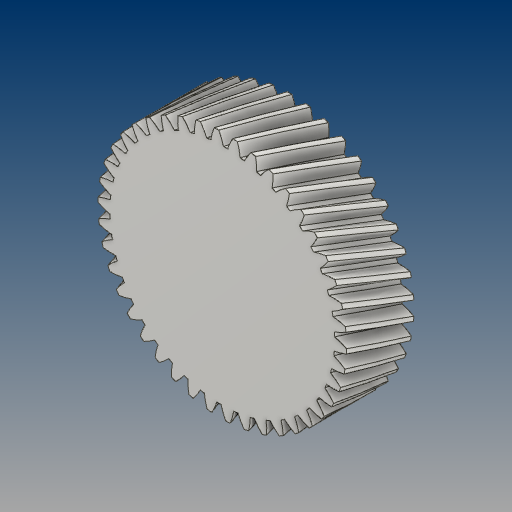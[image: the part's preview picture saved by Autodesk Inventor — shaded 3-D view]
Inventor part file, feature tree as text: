
AUTODESK INVENTOR PART (.ipt)
format: ipt  version: 2021 (Build 250183000, 183)  size: 704,512 bytes
history: native  units: mm (DEFAULTED — no unit token found)
features: plane x3, other x3, sketch x2, extrude x1
ambient origin geometry x8: Origin, YZ Plane, XZ Plane, XY Plane, X Axis, Y Axis, Z Axis, Center Point
bodies: Solid1 (feature_tree)
feature tree (9):
  extrude  "Extrusion1"  Depth=15.0mm TaperAngle=0.0deg
  plane  "Work Plane2"
  plane  "Work Plane8"
  plane  "Work Plane9"
  other  "Spur Gear"
  sketch  "Sketch1"  dims[d0=55.253778mm d1=15.0mm d2=0.0mm]
  sketch  "Sketch2"  dims[d3=55.869333mm d4=10.0mm d5=0.0mm d16=45.0mm d17=0.0mm d34=0.747998mm d39=0.0mm d41=0.0mm d43=45.0mm d46=45.0mm d47=0.0mm d48=0.0mm]
  other  "Srf1"
  other  "Pitch Diameter"
